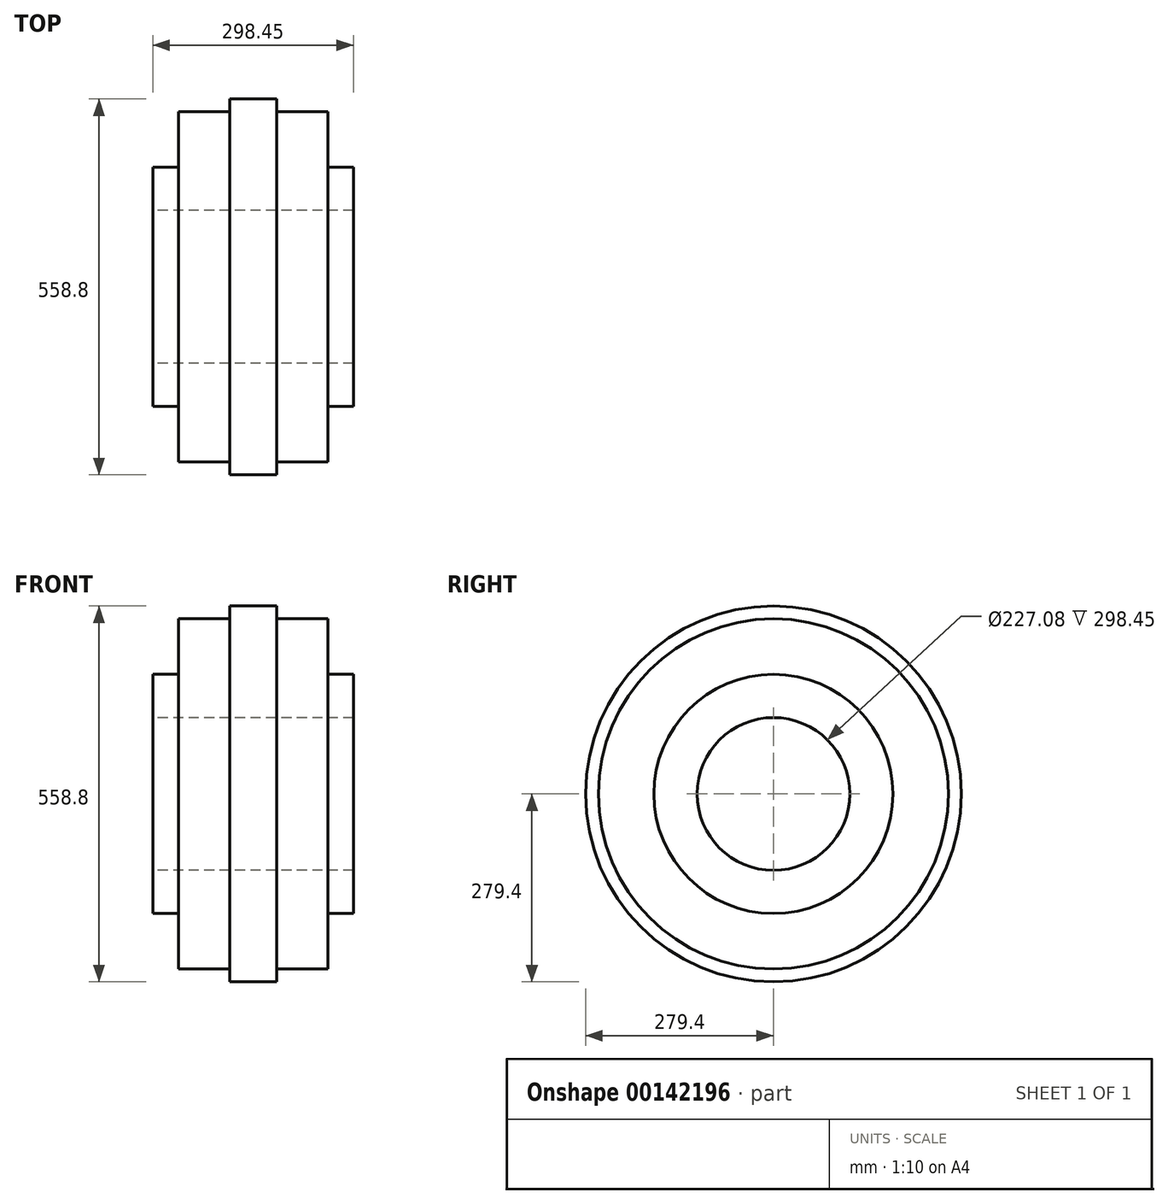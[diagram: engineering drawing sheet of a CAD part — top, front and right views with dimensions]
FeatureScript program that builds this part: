
annotation { "Feature Type Name" : "Feature", "Feature Type Description" : "" }
export const myFeature = defineFeature(function(context is Context, id is Id, definition is map)
    precondition{}
    {
        {
            var Q0;
            Q0=qCreatedBy(makeId("Top.planeOp"),FACE);
            var sketch = newSketch(context, id + "F0", { "sketchPlane" : qUnion([Q0])});
            skLineSegment(sketch, "E0", {"start": v(0, 0) * mm, "end": v(460.11, 0) * mm, "construction": true});
            skLineSegment(sketch, "E1", {"start": v(0, 177.8) * mm, "end": v(38.1, 177.8) * mm});
            skLineSegment(sketch, "E2", {"start": v(38.1, 177.8) * mm, "end": v(38.1, 260.35) * mm});
            skLineSegment(sketch, "E3", {"start": v(38.1, 260.35) * mm, "end": v(114.3, 260.35) * mm});
            skLineSegment(sketch, "E4", {"start": v(114.3, 260.35) * mm, "end": v(114.3, 279.4) * mm});
            skLineSegment(sketch, "E5", {"start": v(114.3, 279.4) * mm, "end": v(184.15, 279.4) * mm});
            skLineSegment(sketch, "E6", {"start": v(184.15, 279.4) * mm, "end": v(184.15, 260.35) * mm});
            skLineSegment(sketch, "E7", {"start": v(184.15, 260.35) * mm, "end": v(260.35, 260.35) * mm});
            skLineSegment(sketch, "E8", {"start": v(260.35, 260.35) * mm, "end": v(260.35, 177.8) * mm});
            skLineSegment(sketch, "E9", {"start": v(260.35, 177.8) * mm, "end": v(298.45, 177.8) * mm});
            skLineSegment(sketch, "E10", {"start": v(298.45, 177.8) * mm, "end": v(298.45, 113.54) * mm});
            skLineSegment(sketch, "E11", {"start": v(298.45, 113.54) * mm, "end": v(0, 113.54) * mm});
            skLineSegment(sketch, "E12", {"start": v(0, 113.54) * mm, "end": v(0, 177.8) * mm});
            skSolve(sketch);
        }
        {
            var Q0;
            Q0 = qSketchRegion(id + "F0", true);
            var Q1;
            Q1=sQuery(id+"F0.wireOp",EDGE,"E0");
            revolve(context, id + "F1", {"entities" : qUnion([Q0]), "axis" : qUnion([Q1]), "revolveType" : RevolveType.FULL});
        }
    });
